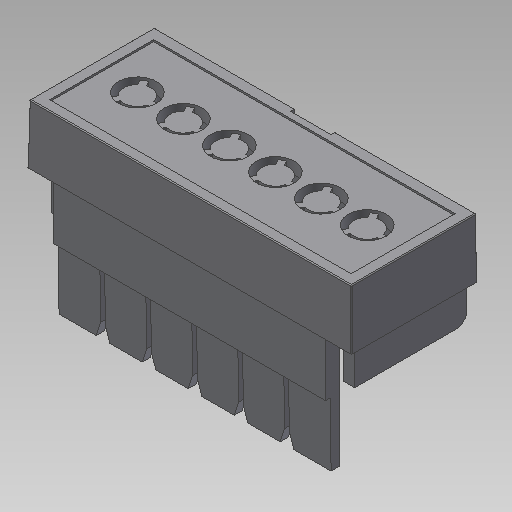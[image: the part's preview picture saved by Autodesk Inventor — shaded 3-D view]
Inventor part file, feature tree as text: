
AUTODESK INVENTOR PART (.ipt)
format: ipt  version: 2018 (Build 220112000, 112)  size: 464,384 bytes
history: native  units: mm
features: sketch x14, extrude x12, projected_geometry x6, other x3, fillet x2, loft x1
ambient origin geometry x8: Origin, YZ Plane, XZ Plane, XY Plane, X Axis, Y Axis, Z Axis, Center Point
bodies: Body1 (feature_tree)
feature tree (38):
  other  "Твердое тело1"
  sketch  "Эскиз1"
  other  "РабПлоскость1"
  loft  "Лофт1"
  extrude  "Выдавливание1"  Depth=35.8mm
  extrude  "Выдавливание2"  Depth=6.5mm
  extrude  "Выдавливание3"  Depth=13.8mm
  extrude  "Выдавливание4"  Depth=35.57mm
  extrude  "Выдавливание5"  TaperAngle=0.0deg  [1 undecoded]
  extrude  "Выдавливание6"  TaperAngle=0.0deg  [1 undecoded]
  extrude  "Выдавливание7"  Depth=1.0mm
  extrude  "Выдавливание8"  Depth=5.5mm
  extrude  "Выдавливание9"  Depth=4.5mm
  extrude  "Выдавливание10"  Depth=0.5mm TaperAngle=0.0deg
  extrude  "Выдавливание11"  Depth=11.5mm
  extrude  "Выдавливание12"  Depth=33.3mm
  fillet  "Сопряжение6"  Radius=0.2mm
  fillet  "Сопряжение7"  Radius=4.2mm
  sketch  "Эскиз2"
  sketch  "Эскиз3"
  sketch  "Эскиз4"
  sketch  "Эскиз5"
  sketch  "Эскиз6"
  projected_geometry  "Спроецированная петля1"
  projected_geometry  "Спроецированная петля2"
  projected_geometry  "Спроецированная петля3"
  projected_geometry  "Спроецированная петля4"
  projected_geometry  "Спроецированная петля5"
  projected_geometry  "Спроецированная петля6"
  sketch  "Эскиз7"
  sketch  "Эскиз8"
  sketch  "Эскиз9"
  sketch  "Эскиз10"
  sketch  "Эскиз11"
  sketch  "Эскиз12"
  sketch  "Эскиз13"
  sketch  "Эскиз14"
  other  "Проецирование ребер1"
note: 2 required parameter values undecoded (feature->parameter linkage not recoverable at this tier; creation-order binding heuristic only, values carry confidence <= 0.55)
